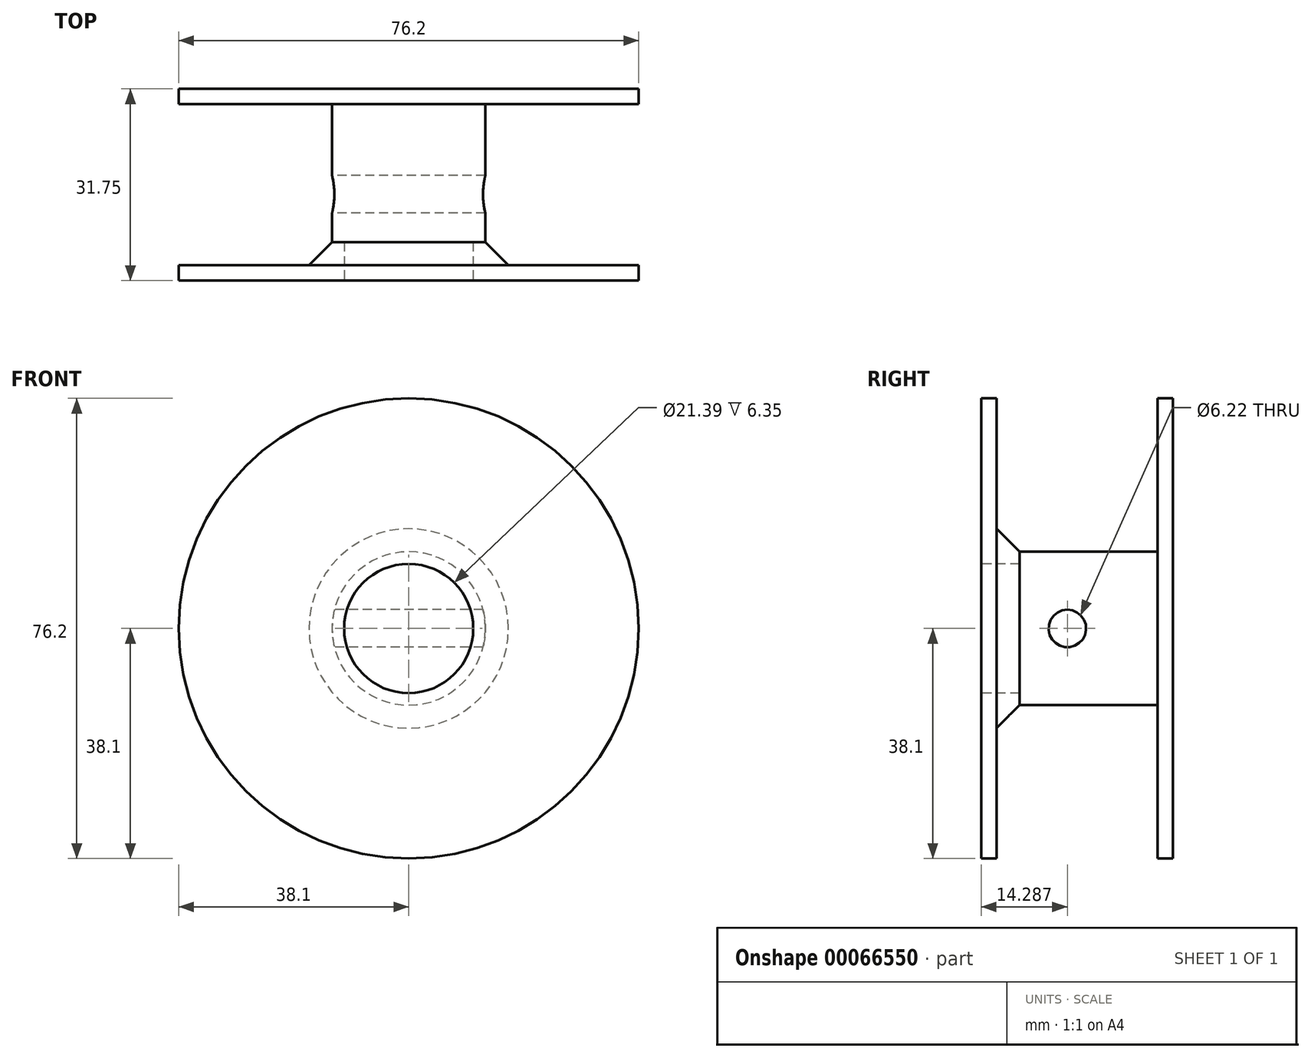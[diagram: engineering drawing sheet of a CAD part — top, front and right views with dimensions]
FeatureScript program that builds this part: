
annotation { "Feature Type Name" : "Feature", "Feature Type Description" : "" }
export const myFeature = defineFeature(function(context is Context, id is Id, definition is map)
    precondition{}
    {
        {
            var Q0;
            Q0=qCreatedBy(makeId("Front.planeOp"),FACE);
            var sketch = newSketch(context, id + "F0", { "sketchPlane" : qUnion([Q0])});
            skCircle(sketch, "E0", {"center": v(0, 0) * mm, "radius": 38.1 * mm});
            skSolve(sketch);
        }
        {
            var Q0;
            Q0 = qSketchRegion(id + "F0", true);
            extrude(context, id + "F1", {"entities" : qUnion([Q0]), "oppositeDirection" : true, "depth" : 2.54 * mm});
        }
        {
            var Q0;
            Q0=qCreatedBy(makeId("Front.planeOp"),FACE);
            var sketch = newSketch(context, id + "F2", { "sketchPlane" : qUnion([Q0])});
            skCircle(sketch, "E1", {"center": v(0, 0) * mm, "radius": 12.7 * mm});
            skSolve(sketch);
        }
        {
            var Q0;
            Q0 = qSketchRegion(id + "F2", true);
            extrude(context, id + "F3", {"entities" : qUnion([Q0]), "operationType" : NewBodyOperationType.ADD, "oppositeDirection" : true, "depth" : 29.2 * mm});
        }
        {
            var Q0;
            Q0=qCreatedBy(makeId("Front.planeOp"),FACE);
            var sketch = newSketch(context, id + "F4", { "sketchPlane" : qUnion([Q0])});
            skCircle(sketch, "E2", {"center": v(0, 0) * mm, "radius": 10.7 * mm});
            skSolve(sketch);
        }
        {
            var Q0;
            Q0=makeQuery(id+"F4.imprint","IMPRINT",FACE,{"disambiguationData":[TD([[makeQuery(id+"F4.imprint","IMPRINT",EDGE,{"derivedFrom":sQuery(id+"F4.wireOp",EDGE,"E2")}),1.0]])]});
            extrude(context, id + "F5", {"entities" : qUnion([Q0]), "operationType" : NewBodyOperationType.REMOVE, "oppositeDirection" : true, "depth" : 6.35 * mm});
        }
        {
            var Q0;
            Q0=makeQuery(id+"F3.opExtrude","CAP_FACE",FACE,{"disambiguationData":[OSD([sQuery(id+"F2.wireOp",EDGE,"E1")])],"isStart":false});
            var sketch = newSketch(context, id + "F6", { "sketchPlane" : qUnion([Q0])});
            skCircle(sketch, "E3", {"center": v(0, 0) * mm, "radius": 38.1 * mm});
            skSolve(sketch);
        }
        {
            var Q0;
            Q0 = qSketchRegion(id + "F6", true);
            extrude(context, id + "F7", {"entities" : qUnion([Q0]), "operationType" : NewBodyOperationType.ADD, "depth" : 2.54 * mm});
        }
        {
            var Q0;
            Q0=qCreatedBy(makeId("Right.planeOp"),FACE);
            var sketch = newSketch(context, id + "F8", { "sketchPlane" : qUnion([Q0])});
            skCircle(sketch, "E4", {"center": v(14.29, 0) * mm, "radius": 3.11 * mm});
            skSolve(sketch);
        }
        {
            var Q0;
            Q0 = qSketchRegion(id + "F8", true);
            extrude(context, id + "F9", {"entities" : qUnion([Q0]), "operationType" : NewBodyOperationType.REMOVE, "depth" : 25.4 * mm, "hasSecondDirection" : true, "secondDirectionOppositeDirection" : true, "secondDirectionDepth" : 25.4 * mm});
        }
        {
            var Q0;
            Q0=makeQuery(id+"F3.boolean.opBoolean","INTERSECT",EDGE,{"derivedFrom":[makeQuery(id+"F1.opExtrude","CAP_FACE",FACE,{"disambiguationData":[OSD([sQuery(id+"F0.wireOp",EDGE,"E0")])],"isStart":false}),makeQuery(id+"F3.opExtrude","SWEPT_FACE",FACE,{"disambiguationData":[OSD([sQuery(id+"F2.wireOp",EDGE,"E1")])]})]});
            chamfer(context, id + "F10", {"entities" : qUnion([Q0]), "width" : 3.8 * mm, "tangentPropagation" : true});
        }
    });
